# Revit family: LeeSti Corner
name_source: partatom
category: Lighting Fixtures
revit_build: Autodesk Revit 2017 (Build: 20160225_1515(x64)
units: mm (PartAtom-declared; Revit-internal decimal feet)

## family parameters
Always vertical = Yes
Cut with Voids When Loaded = No
Light Source = Yes
OmniClass Number = 23.80.70.00
OmniClass Title = Lighting
Part Type = Normal
Room Calculation Point = No
Round Connector Dimension = Use Diameter
Shared = No
Work Plane-Based = No

## types (7) — shared parameters
AngleLeftside = 45.00°
AngleRightside = 45.00°
Color Filter = 16777215
Dimming Lamp Color Temperature Shift = <None>

## per-type parameters (varying)
| type | Emit from Line Length | LED module | Light Source Symbol Size |
| 2ft nominal | 2' - 0" | 2' - 0" | 2' - 0" |
| 3ft nominal | 2' - 10 1/2" | 2' - 10 1/2" | 2' - 10 1/2" |
| 4ft nominal | 3' - 10 1/2" | 3' - 10 1/2" | 3' - 10 1/2" |
| 5ft nominal | 4' - 9" | 4' - 9" | 4' - 9" |
| 6ft nominal | 5' - 9" | 5' - 9" | 5' - 9" |
| 7ft nominal | 6' - 7 1/2" | 6' - 7 1/2" | 6' - 7 1/2" |
| 8ft nominal | 7' - 7 1/2" | 7' - 7 1/2" | 7' - 7 1/2" |

## geometry (parser evidence)
native form markers: Sweep x2
no freeform markers — native parametric forms only
